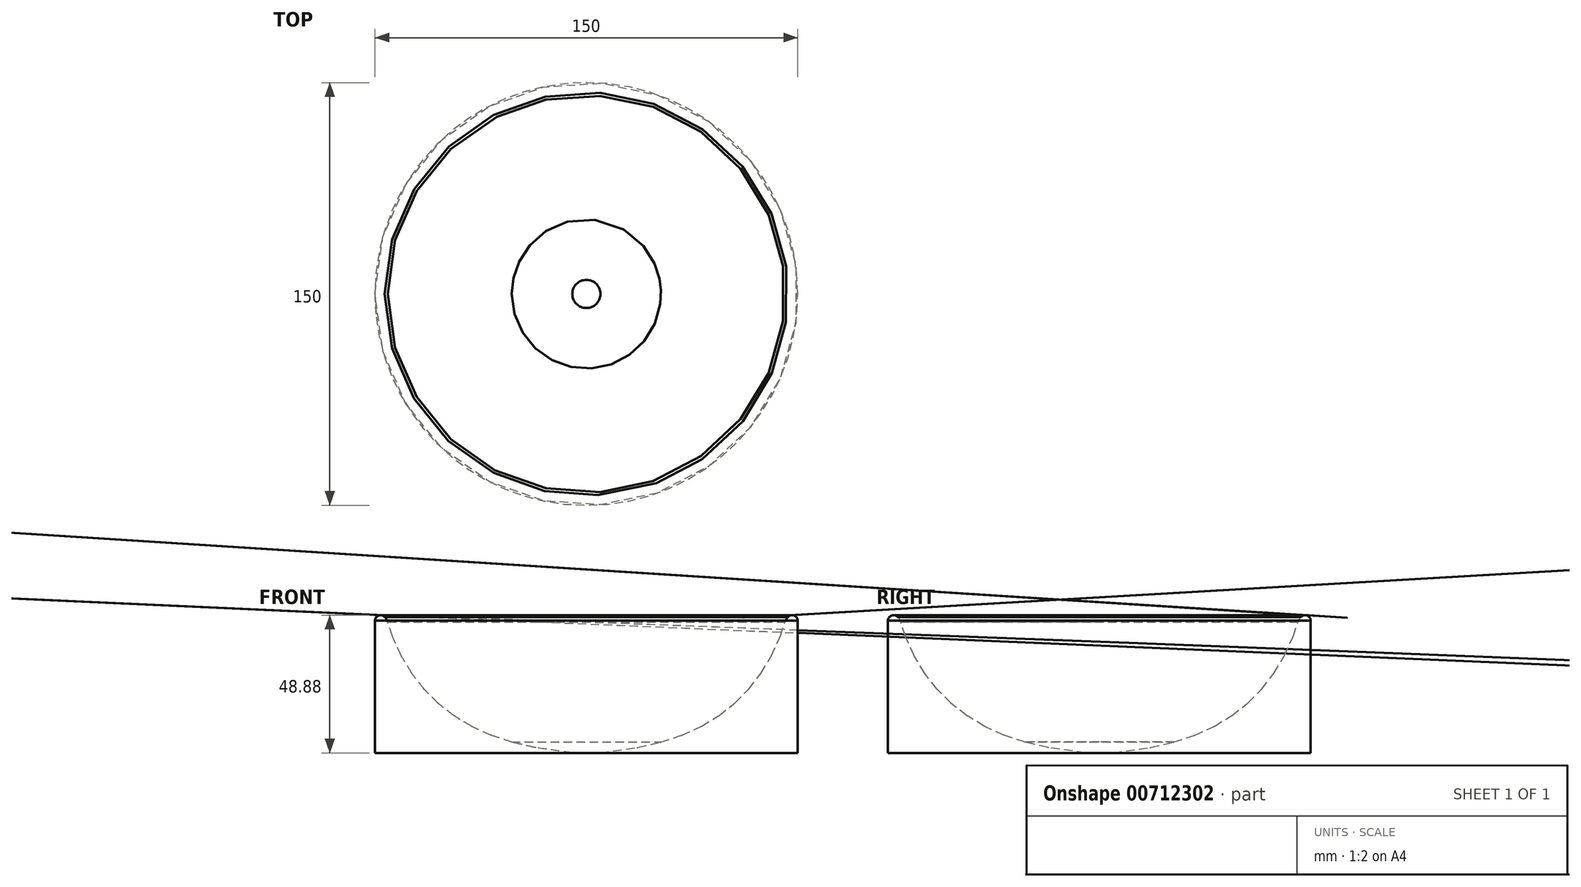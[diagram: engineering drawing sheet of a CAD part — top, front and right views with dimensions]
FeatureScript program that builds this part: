
annotation { "Feature Type Name" : "Feature", "Feature Type Description" : "" }
export const myFeature = defineFeature(function(context is Context, id is Id, definition is map)
    precondition{}
    {
        {
            var Q0;
            Q0=qCreatedBy(makeId("Front.planeOp"),FACE);
            var sketch = newSketch(context, id + "F0", { "sketchPlane" : qUnion([Q0])});
            skLineSegment(sketch, "E0.top", {"start": v(-50, -37.5) * mm, "end": v(20.6, -37.5) * mm});
            skPoint(sketch, "E0.middle", {"position": v(0, 0) * mm});
            skPoint(sketch, "E1", {"position": v(-50, 37.5) * mm});
            skPoint(sketch, "E2.0.1.0", {"position": v(-50, 32.5) * mm});
            skPoint(sketch, "E2.0.2.0", {"position": v(-50, 27.5) * mm});
            skPoint(sketch, "E2.0.3.0", {"position": v(-50, 22.5) * mm});
            skPoint(sketch, "E2.0.4.0", {"position": v(-50, 17.5) * mm});
            skPoint(sketch, "E2.0.5.0", {"position": v(-50, 12.5) * mm});
            skPoint(sketch, "E2.0.6.0", {"position": v(-50, 7.5) * mm});
            skPoint(sketch, "E2.0.7.0", {"position": v(-50, 2.5) * mm});
            skPoint(sketch, "E2.0.8.0", {"position": v(-50, -2.5) * mm});
            skPoint(sketch, "E2.0.9.0", {"position": v(-50, -7.5) * mm});
            skPoint(sketch, "E2.0.10.0", {"position": v(-50, -12.5) * mm});
            skPoint(sketch, "E2.0.11.0", {"position": v(-50, -17.5) * mm});
            skPoint(sketch, "E2.0.12.0", {"position": v(-50, -22.5) * mm});
            skPoint(sketch, "E2.0.13.0", {"position": v(-50, -27.5) * mm});
            skPoint(sketch, "E2.0.14.0", {"position": v(-50, -32.5) * mm});
            skPoint(sketch, "E3", {"position": v(-50, -37.5) * mm});
            skPoint(sketch, "E4.1.0.0", {"position": v(-45, -37.5) * mm});
            skPoint(sketch, "E4.2.0.0", {"position": v(-40, -37.5) * mm});
            skPoint(sketch, "E4.3.0.0", {"position": v(-35, -37.5) * mm});
            skPoint(sketch, "E4.4.0.0", {"position": v(-30, -37.5) * mm});
            skPoint(sketch, "E4.5.0.0", {"position": v(-25, -37.5) * mm});
            skPoint(sketch, "E4.6.0.0", {"position": v(-20, -37.5) * mm});
            skPoint(sketch, "E4.7.0.0", {"position": v(-15, -37.5) * mm});
            skPoint(sketch, "E4.8.0.0", {"position": v(-10, -37.5) * mm});
            skPoint(sketch, "E4.9.0.0", {"position": v(-5, -37.5) * mm});
            skPoint(sketch, "E4.10.0.0", {"position": v(0, -37.5) * mm});
            skPoint(sketch, "E4.11.0.0", {"position": v(5, -37.5) * mm});
            skPoint(sketch, "E4.12.0.0", {"position": v(10, -37.5) * mm});
            skPoint(sketch, "E4.13.0.0", {"position": v(15, -37.5) * mm});
            skPoint(sketch, "E4.14.0.0", {"position": v(20, -37.5) * mm});
            skPoint(sketch, "E4.15.0.0", {"position": v(25, -37.5) * mm});
            skPoint(sketch, "E4.16.0.0", {"position": v(30, -37.5) * mm});
            skPoint(sketch, "E4.17.0.0", {"position": v(35, -37.5) * mm});
            skPoint(sketch, "E4.18.0.0", {"position": v(40, -37.5) * mm});
            skPoint(sketch, "E4.19.0.0", {"position": v(45, -37.5) * mm});
            skLineSegment(sketch, "E4.direction1", {"start": v(-50, -37.5) * mm, "end": v(-45, -37.5) * mm, "construction": true});
            skLineSegment(sketch, "E5", {"start": v(-40.62, -3.13) * mm, "end": v(-36.88, -9.37) * mm});
            skLineSegment(sketch, "E6", {"start": v(-32.5, -15) * mm, "end": v(-27.5, -20) * mm});
            skLineSegment(sketch, "E7", {"start": v(-46.25, 11.25) * mm, "end": v(-43.75, 3.75) * mm});
            skLineSegment(sketch, "E8", {"start": v(-43.75, 3.75) * mm, "end": v(-40.62, -3.13) * mm});
            skLineSegment(sketch, "E9", {"start": v(-36.87, -9.37) * mm, "end": v(-32.5, -15) * mm});
            skLineSegment(sketch, "E10", {"start": v(-27.5, -20) * mm, "end": v(-21.87, -24.38) * mm});
            skLineSegment(sketch, "E11", {"start": v(-21.87, -24.38) * mm, "end": v(-15.63, -28.12) * mm});
            skLineSegment(sketch, "E12", {"start": v(-8.75, -31.25) * mm, "end": v(-1.25, -33.75) * mm});
            skLineSegment(sketch, "E13", {"start": v(-1.25, -33.75) * mm, "end": v(6.87, -35.62) * mm});
            skLineSegment(sketch, "E14.trimOffspring", {"start": v(19.4, -37.41) * mm, "end": v(20.6, -37.5) * mm});
            skLineSegment(sketch, "E15.trimOffspring", {"start": v(6.87, -35.62) * mm, "end": v(20, -37.5) * mm});
            skLineSegment(sketch, "E16.trimOffspring", {"start": v(-15.63, -28.12) * mm, "end": v(-8.75, -31.25) * mm});
            skPoint(sketch, "E17.orphan", {"position": v(50, 37.5) * mm});
            skPoint(sketch, "E18.trimOffspring.end.orphan", {"position": v(50, -37.5) * mm});
            skLineSegment(sketch, "E19", {"start": v(-46.25, 11.25) * mm, "end": v(-50, 12.5) * mm});
            skLineSegment(sketch, "E20.trimOffspring", {"start": v(-50, 12.5) * mm, "end": v(-50, -37.5) * mm});
            skLineSegment(sketch, "E21", {"start": v(25, -37.5) * mm, "end": v(25, 21.38) * mm, "construction": true});
            skSolve(sketch);
        }
        {
            var Q0;
            Q0=makeQuery(id+"F0.imprint","IMPRINT",FACE,{"disambiguationData":[TD([[makeQuery(id+"F0.imprint","IMPRINT",EDGE,{"derivedFrom":sQuery(id+"F0.wireOp",EDGE,"E5")}),-1.0]])]});
            var Q1;
            Q1=sQuery(id+"F0.wireOp",EDGE,"E21");
            revolve(context, id + "F1", {"surfaceOperationType" : NewSurfaceOperationType.NEW, "entities" : qUnion([Q0]), "axis" : qUnion([Q1]), "revolveType" : RevolveType.FULL});
        }
        {
            var Q0;
            Q0=makeQuery(id+"F1.opRevolve","SWEPT_EDGE",EDGE,{"disambiguationData":[OSD([sQuery(id+"F0.wireOp",EDGE,"E7"),sQuery(id+"F0.wireOp",EDGE,"E8")])]});
            var Q1;
            Q1=makeQuery(id+"F1.opRevolve","SWEPT_EDGE",EDGE,{"disambiguationData":[OSD([sQuery(id+"F0.wireOp",EDGE,"E5"),sQuery(id+"F0.wireOp",EDGE,"E8")])]});
            var Q2;
            Q2=makeQuery(id+"F1.opRevolve","SWEPT_EDGE",EDGE,{"disambiguationData":[OSD([sQuery(id+"F0.wireOp",EDGE,"E5"),sQuery(id+"F0.wireOp",EDGE,"E9")])]});
            var Q3;
            Q3=makeQuery(id+"F1.opRevolve","SWEPT_EDGE",EDGE,{"disambiguationData":[OSD([sQuery(id+"F0.wireOp",EDGE,"E6"),sQuery(id+"F0.wireOp",EDGE,"E9")])]});
            var Q4;
            Q4=makeQuery(id+"F1.opRevolve","SWEPT_EDGE",EDGE,{"disambiguationData":[OSD([sQuery(id+"F0.wireOp",EDGE,"E6"),sQuery(id+"F0.wireOp",EDGE,"E10")])]});
            var Q5;
            Q5=makeQuery(id+"F1.opRevolve","SWEPT_EDGE",EDGE,{"disambiguationData":[OSD([sQuery(id+"F0.wireOp",EDGE,"E10"),sQuery(id+"F0.wireOp",EDGE,"E11")])]});
            var Q6;
            Q6=makeQuery(id+"F1.opRevolve","SWEPT_EDGE",EDGE,{"disambiguationData":[OSD([sQuery(id+"F0.wireOp",EDGE,"E11"),sQuery(id+"F0.wireOp",EDGE,"E16.trimOffspring")])]});
            var Q7;
            Q7=makeQuery(id+"F1.opRevolve","SWEPT_EDGE",EDGE,{"disambiguationData":[OSD([sQuery(id+"F0.wireOp",EDGE,"E12"),sQuery(id+"F0.wireOp",EDGE,"E16.trimOffspring")])]});
            var Q8;
            Q8=makeQuery(id+"F1.opRevolve","SWEPT_EDGE",EDGE,{"disambiguationData":[OSD([sQuery(id+"F0.wireOp",EDGE,"E12"),sQuery(id+"F0.wireOp",EDGE,"E13")])]});
            var Q9;
            Q9=makeQuery(id+"F1.opRevolve","SWEPT_EDGE",EDGE,{"disambiguationData":[OSD([sQuery(id+"F0.wireOp",EDGE,"E13"),sQuery(id+"F0.wireOp",EDGE,"E15.trimOffspring")])]});
            var Q10;
            Q10=makeQuery(id+"F1.opRevolve","SWEPT_EDGE",EDGE,{"disambiguationData":[OSD([sQuery(id+"F0.wireOp",EDGE,"E7"),sQuery(id+"F0.wireOp",EDGE,"E19")])]});
            fillet(context, id + "F2", {"entities" : qUnion([Q0, Q1, Q2, Q3, Q4, Q5, Q6, Q7, Q8, Q9, Q10]), "radius" : 5 * mm, "tangentPropagation" : true, "rho" : 0.5, "crossSection" : FilletCrossSection.CONIC, "allowEdgeOverflow" : false});
        }
        {
            var Q0;
            Q0=makeQuery(id+"F1.opRevolve","SWEPT_EDGE",EDGE,{"disambiguationData":[OSD([sQuery(id+"F0.wireOp",EDGE,"E19"),sQuery(id+"F0.wireOp",EDGE,"E20.trimOffspring")])]});
            fillet(context, id + "F3", {"entities" : qUnion([Q0]), "radius" : 2 * mm, "tangentPropagation" : true, "allowEdgeOverflow" : false});
        }
    });
